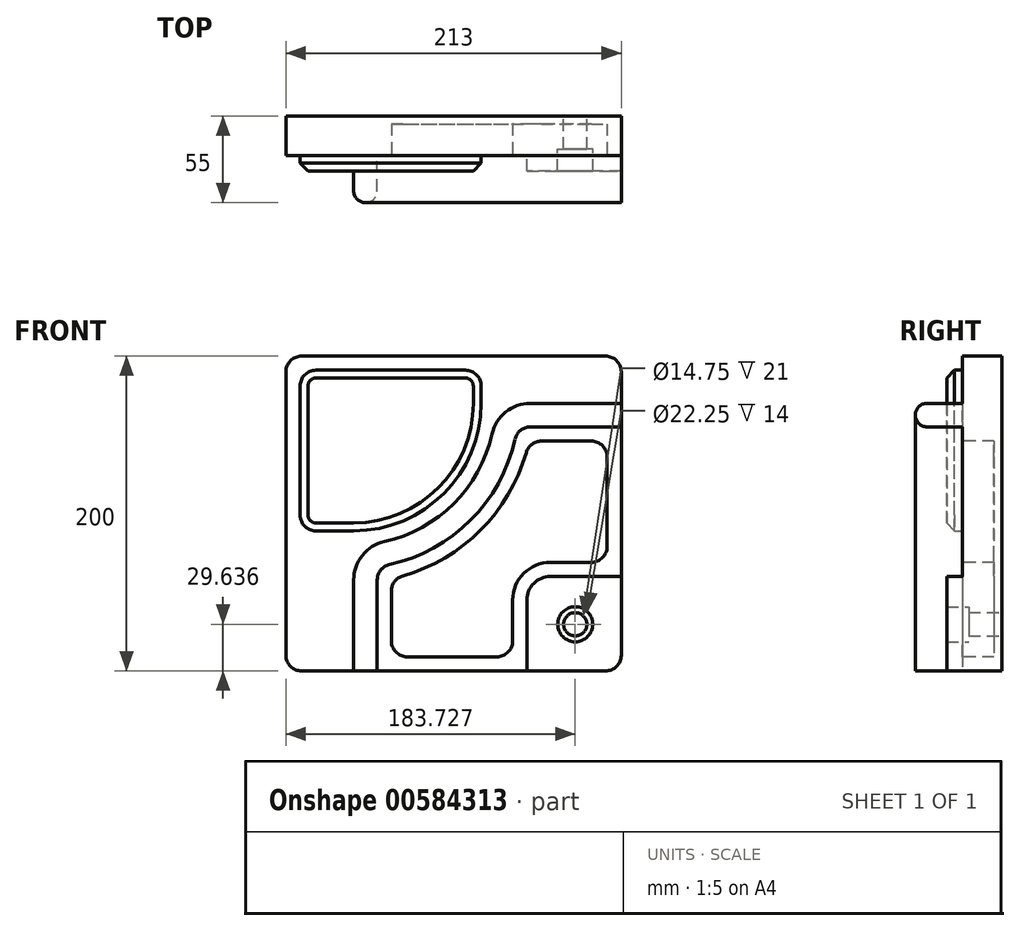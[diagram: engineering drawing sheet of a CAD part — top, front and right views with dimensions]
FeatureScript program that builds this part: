
annotation { "Feature Type Name" : "Feature", "Feature Type Description" : "" }
export const myFeature = defineFeature(function(context is Context, id is Id, definition is map)
    precondition{}
    {
        {
            var Q0;
            Q0=qCreatedBy(makeId("Front.planeOp"),FACE);
            var sketch = newSketch(context, id + "F0", { "sketchPlane" : qUnion([Q0])});
            skLineSegment(sketch, "E0.bottom", {"start": v(-96.5, 100) * mm, "end": v(96.5, 100) * mm});
            skLineSegment(sketch, "E0.top", {"start": v(-96.5, -100) * mm, "end": v(96.5, -100) * mm});
            skLineSegment(sketch, "E0.left", {"start": v(-106.5, 90) * mm, "end": v(-106.5, -90) * mm});
            skLineSegment(sketch, "E0.right", {"start": v(106.5, 90) * mm, "end": v(106.5, -90) * mm});
            skPoint(sketch, "E0.middle", {"position": v(0, 0) * mm});
            skPoint(sketch, "E1.visualSharp", {"position": v(-106.5, 100) * mm});
            skArc(sketch, "E1.filletArc", {"start": v(-96.5, 100) * mm, "mid": v(-103.57, 97.07) * mm, "end": v(-106.5, 90) * mm});
            skPoint(sketch, "E2.visualSharp", {"position": v(106.5, 100) * mm});
            skArc(sketch, "E2.filletArc", {"start": v(106.5, 90) * mm, "mid": v(103.57, 97.07) * mm, "end": v(96.5, 100) * mm});
            skPoint(sketch, "E3.visualSharp", {"position": v(106.5, -100) * mm});
            skArc(sketch, "E3.filletArc", {"start": v(96.5, -100) * mm, "mid": v(103.57, -97.07) * mm, "end": v(106.5, -90) * mm});
            skPoint(sketch, "E4.visualSharp", {"position": v(-106.5, -100) * mm});
            skArc(sketch, "E4.filletArc", {"start": v(-106.5, -90) * mm, "mid": v(-103.57, -97.07) * mm, "end": v(-96.5, -100) * mm});
            skLineSegment(sketch, "E5.bottom", {"start": v(106.5, -40) * mm, "end": v(61.5, -40) * mm});
            skLineSegment(sketch, "E5.top", {"start": v(96.5, -100) * mm, "end": v(46.5, -100) * mm});
            skLineSegment(sketch, "E5.left", {"start": v(106.5, -40) * mm, "end": v(106.5, -90) * mm});
            skLineSegment(sketch, "E5.right", {"start": v(46.5, -55) * mm, "end": v(46.5, -100) * mm});
            skLineSegment(sketch, "E6.bottom", {"start": v(48.75, 70) * mm, "end": v(106.5, 70) * mm});
            skLineSegment(sketch, "E6.left", {"start": v(-63.5, -42.25) * mm, "end": v(-63.5, -100) * mm});
            skPoint(sketch, "E6.middle", {"position": v(63.73, -49.49) * mm});
            skPoint(sketch, "E7.visualSharp", {"position": v(46.5, -40) * mm});
            skArc(sketch, "E7.filletArc", {"start": v(61.5, -40) * mm, "mid": v(50.9, -44.4) * mm, "end": v(46.5, -55) * mm});
            skArc(sketch, "E8", {"start": v(-43.93, -17.85) * mm, "mid": v(0.14, 6.36) * mm, "end": v(24.35, 50.43) * mm});
            skPoint(sketch, "E9.visualSharp", {"position": v(26.5, 70) * mm});
            skArc(sketch, "E9.filletArc", {"start": v(48.75, 70) * mm, "mid": v(33.11, 64.5) * mm, "end": v(24.35, 50.43) * mm});
            skPoint(sketch, "E10.visualSharp", {"position": v(-63.5, -20) * mm});
            skArc(sketch, "E10.filletArc", {"start": v(-43.93, -17.85) * mm, "mid": v(-58, -26.61) * mm, "end": v(-63.5, -42.25) * mm});
            skLineSegment(sketch, "E11.0", {"start": v(48.75, 55) * mm, "end": v(106.5, 55) * mm});
            skLineSegment(sketch, "E11.1", {"start": v(-48.5, -42.25) * mm, "end": v(-48.5, -100) * mm});
            skArc(sketch, "E11.2", {"start": v(-40.67, -32.49) * mm, "mid": v(-46.3, -36) * mm, "end": v(-48.5, -42.25) * mm});
            skArc(sketch, "E11.3", {"start": v(-40.67, -32.49) * mm, "mid": v(10.75, -4.25) * mm, "end": v(38.99, 47.17) * mm});
            skArc(sketch, "E11.4", {"start": v(48.75, 55) * mm, "mid": v(42.5, 52.8) * mm, "end": v(38.99, 47.17) * mm});
            skPoint(sketch, "E12", {"position": v(76.5, -70) * mm});
            skLineSegment(sketch, "E13.0", {"start": v(55.75, 46) * mm, "end": v(87.5, 46) * mm});
            skArc(sketch, "E13.1", {"start": v(-32.24, -39.63) * mm, "mid": v(17.11, -10.61) * mm, "end": v(46.13, 38.74) * mm});
            skLineSegment(sketch, "E13.2", {"start": v(-39.5, -49.25) * mm, "end": v(-39.5, -81) * mm});
            skLineSegment(sketch, "E14.0", {"start": v(37.5, -55) * mm, "end": v(37.5, -81) * mm});
            skArc(sketch, "E15.0", {"start": v(61.5, -31) * mm, "mid": v(44.53, -38.03) * mm, "end": v(37.5, -55) * mm});
            skLineSegment(sketch, "E16.0", {"start": v(87.5, -31) * mm, "end": v(61.5, -31) * mm});
            skLineSegment(sketch, "E17.trimOffspring", {"start": v(97.5, 36) * mm, "end": v(97.5, -21) * mm});
            skLineSegment(sketch, "E18.trimOffspring", {"start": v(-29.5, -91) * mm, "end": v(27.5, -91) * mm});
            skPoint(sketch, "E19.visualSharp", {"position": v(97.5, 46) * mm});
            skArc(sketch, "E19.filletArc", {"start": v(97.5, 36) * mm, "mid": v(94.57, 43.07) * mm, "end": v(87.5, 46) * mm});
            skPoint(sketch, "E20.visualSharp", {"position": v(37.5, -91) * mm});
            skArc(sketch, "E20.filletArc", {"start": v(27.5, -91) * mm, "mid": v(34.57, -88.07) * mm, "end": v(37.5, -81) * mm});
            skPoint(sketch, "E21.visualSharp", {"position": v(97.5, -31) * mm});
            skArc(sketch, "E21.filletArc", {"start": v(87.5, -31) * mm, "mid": v(94.57, -28.07) * mm, "end": v(97.5, -21) * mm});
            skPoint(sketch, "E22.visualSharp", {"position": v(47.95, 46) * mm});
            skArc(sketch, "E22.filletArc", {"start": v(55.75, 46) * mm, "mid": v(49.72, 43.98) * mm, "end": v(46.13, 38.74) * mm});
            skPoint(sketch, "E23.visualSharp", {"position": v(-39.5, -41.45) * mm});
            skArc(sketch, "E23.filletArc", {"start": v(-32.24, -39.63) * mm, "mid": v(-37.48, -43.22) * mm, "end": v(-39.5, -49.25) * mm});
            skPoint(sketch, "E24.visualSharp", {"position": v(-39.5, -91) * mm});
            skArc(sketch, "E24.filletArc", {"start": v(-39.5, -81) * mm, "mid": v(-36.57, -88.07) * mm, "end": v(-29.5, -91) * mm});
            skArc(sketch, "E25", {"start": v(-63.5, -11) * mm, "mid": v(-6.22, 12.72) * mm, "end": v(17.5, 70) * mm});
            skLineSegment(sketch, "E26", {"start": v(17.5, 70) * mm, "end": v(17.5, 81) * mm});
            skLineSegment(sketch, "E27", {"start": v(-63.5, -11) * mm, "end": v(-87.5, -11) * mm});
            skLineSegment(sketch, "E28.0", {"start": v(-87.5, 91) * mm, "end": v(7.5, 91) * mm});
            skLineSegment(sketch, "E29.0", {"start": v(-97.5, 81) * mm, "end": v(-97.5, -1) * mm});
            skPoint(sketch, "E30.visualSharp", {"position": v(-97.5, 91) * mm});
            skArc(sketch, "E30.filletArc", {"start": v(-87.5, 91) * mm, "mid": v(-94.57, 88.07) * mm, "end": v(-97.5, 81) * mm});
            skPoint(sketch, "E31.visualSharp", {"position": v(-97.5, -11) * mm});
            skArc(sketch, "E31.filletArc", {"start": v(-97.5, -1) * mm, "mid": v(-94.57, -8.07) * mm, "end": v(-87.5, -11) * mm});
            skPoint(sketch, "E32.visualSharp", {"position": v(17.5, 91) * mm});
            skArc(sketch, "E32.filletArc", {"start": v(17.5, 81) * mm, "mid": v(14.57, 88.07) * mm, "end": v(7.5, 91) * mm});
            skSolve(sketch);
        }
        {
            var Q0;
            Q0 = qSketchRegion(id + "F0", true);
            var Q1;
            Q1=makeQuery(id+"F0.imprint","IMPRINT",FACE,{"disambiguationData":[TD([[makeQuery(id+"F0.imprint","IMPRINT",EDGE,{"derivedFrom":sQuery(id+"F0.wireOp",EDGE,"E25")}),1.0]])]});
            var Q2;
            Q2=makeQuery(id+"F0.imprint","IMPRINT",FACE,{"disambiguationData":[TD([[makeQuery(id+"F0.imprint","IMPRINT",EDGE,{"derivedFrom":sQuery(id+"F0.wireOp",EDGE,"E13.0")}),-1.0]])]});
            extrude(context, id + "F1", {"entities" : qUnion([Q0, Q1, Q2]), "oppositeDirection" : true, "depth" : 25 * mm, "offsetDistance" : 25 * mm});
        }
        {
            var Q0;
            Q0=makeQuery(id+"F0.imprint","IMPRINT",FACE,{"disambiguationData":[TD([[makeQuery(id+"F0.imprint","IMPRINT",EDGE,{"derivedFrom":sQuery(id+"F0.wireOp",EDGE,"E25")}),1.0]])]});
            extrude(context, id + "F2", {"entities" : qUnion([Q0]), "operationType" : NewBodyOperationType.ADD, "depth" : 10 * mm, "offsetDistance" : 25 * mm});
        }
        {
            var Q0;
            {var subQ4=sQuery(id+"F0.wireOp",EDGE,"E6.bottom");Q0=makeQuery(id+"F0.imprint","IMPRINT",FACE,{"disambiguationData":[TD([[makeQuery(id+"F0.imprint","IMPRINT",EDGE,{"derivedFrom":subQ4}),-1.0]])]});}
            extrude(context, id + "F3", {"entities" : qUnion([Q0]), "operationType" : NewBodyOperationType.ADD, "depth" : 30 * mm, "offsetDistance" : 25 * mm});
        }
        {
            var Q0;
            Q0=makeQuery(id+"F0.imprint","IMPRINT",FACE,{"disambiguationData":[TD([[makeQuery(id+"F0.imprint","IMPRINT",EDGE,{"derivedFrom":sQuery(id+"F0.wireOp",EDGE,"E13.0")}),-1.0]])]});
            extrude(context, id + "F4", {"entities" : qUnion([Q0]), "operationType" : NewBodyOperationType.REMOVE, "oppositeDirection" : true, "depth" : 20 * mm, "offsetDistance" : 25 * mm});
        }
        {
            var Q0;
            Q0=makeQuery(id+"F0.imprint","IMPRINT",FACE,{"disambiguationData":[TD([[makeQuery(id+"F0.imprint","IMPRINT",EDGE,{"derivedFrom":sQuery(id+"F0.wireOp",EDGE,"E5.bottom")}),1.0]])]});
            extrude(context, id + "F5", {"entities" : qUnion([Q0]), "operationType" : NewBodyOperationType.ADD, "depth" : 10 * mm, "offsetDistance" : 25 * mm});
        }
        {
            var Q0;
            Q0=makeQuery(id+"F5.opExtrude","CAP_FACE",FACE,{"disambiguationData":[OSD([sQuery(id+"F0.wireOp",EDGE,"E5.bottom"),sQuery(id+"F0.wireOp",EDGE,"E5.top"),sQuery(id+"F0.wireOp",EDGE,"E5.left"),sQuery(id+"F0.wireOp",EDGE,"E5.right"),sQuery(id+"F0.wireOp",EDGE,"E7.filletArc"),sQuery(id+"F0.wireOp",EDGE,"E3.filletArc")])],"isStart":false});
            var sketch = newSketch(context, id + "F6", { "sketchPlane" : qUnion([Q0])});
            skPoint(sketch, "E33", {"position": v(77.23, -70.36) * mm});
            skSolve(sketch);
        }
        {
            var Q0;
            Q0=sQuery(id+"F6.wireOp",VERTEX,"E33");
            var Q1;
            Q1=makeQuery(id+"F1.opExtrude","SWEPT_BODY",BODY,{"disambiguationData":[OSD([sQuery(id+"F0.wireOp",EDGE,"E0.bottom"),sQuery(id+"F0.wireOp",EDGE,"E0.top"),sQuery(id+"F0.wireOp",EDGE,"E0.left"),sQuery(id+"F0.wireOp",EDGE,"E0.right"),sQuery(id+"F0.wireOp",EDGE,"E1.filletArc"),sQuery(id+"F0.wireOp",EDGE,"E2.filletArc"),sQuery(id+"F0.wireOp",EDGE,"E4.filletArc"),sQuery(id+"F0.wireOp",EDGE,"E5.top"),sQuery(id+"F0.wireOp",EDGE,"E5.left"),sQuery(id+"F0.wireOp",EDGE,"E3.filletArc")])]});
            hole(context, id + "F7", {"style" : HoleStyle.C_BORE, "endStyle" : HoleEndStyle.THROUGH, "standardTappedOrClearance" : lookupTablePath({ "standard" : "ISO", "fit" : "Close", "size" : "M14", "type" : "Clearance" }), "standardBlindInLast" : lookupTablePath({ "fit" : "Close", "standard" : "ISO", "size" : "M14", "type" : "Clearance" }), "holeDiameter" : 14.75 * mm, "cBoreDiameter" : 22.25 * mm, "cBoreDepth" : 14 * mm, "majorDiameter" : 5 * mm, "isTappedThrough" : true, "tappedDepth" : 12 * mm, "tapClearance" : 3, "locations" : qUnion([Q0]), "scope" : qUnion([Q1])});
        }
        {
            var Q0;
            Q0=makeQuery(id+"F2.opExtrude","CAP_EDGE",EDGE,{"disambiguationData":[OSD([sQuery(id+"F0.wireOp",EDGE,"E29.0")])],"isStart":false});
            chamfer(context, id + "F8", {"entities" : qUnion([Q0]), "width" : 5 * mm, "tangentPropagation" : true});
        }
        {
            var Q0;
            Q0=makeQuery(id+"F3.opExtrude","CAP_EDGE",EDGE,{"disambiguationData":[OSD([sQuery(id+"F0.wireOp",EDGE,"E6.left")])],"isStart":false});
            var Q1;
            Q1=makeQuery(id+"F3.opExtrude","CAP_EDGE",EDGE,{"disambiguationData":[OSD([sQuery(id+"F0.wireOp",EDGE,"E11.1")])],"isStart":false});
            fillet(context, id + "F9", {"entities" : qUnion([Q0, Q1]), "radius" : 7.5 * mm, "tangentPropagation" : true, "allowEdgeOverflow" : false});
        }
    });
